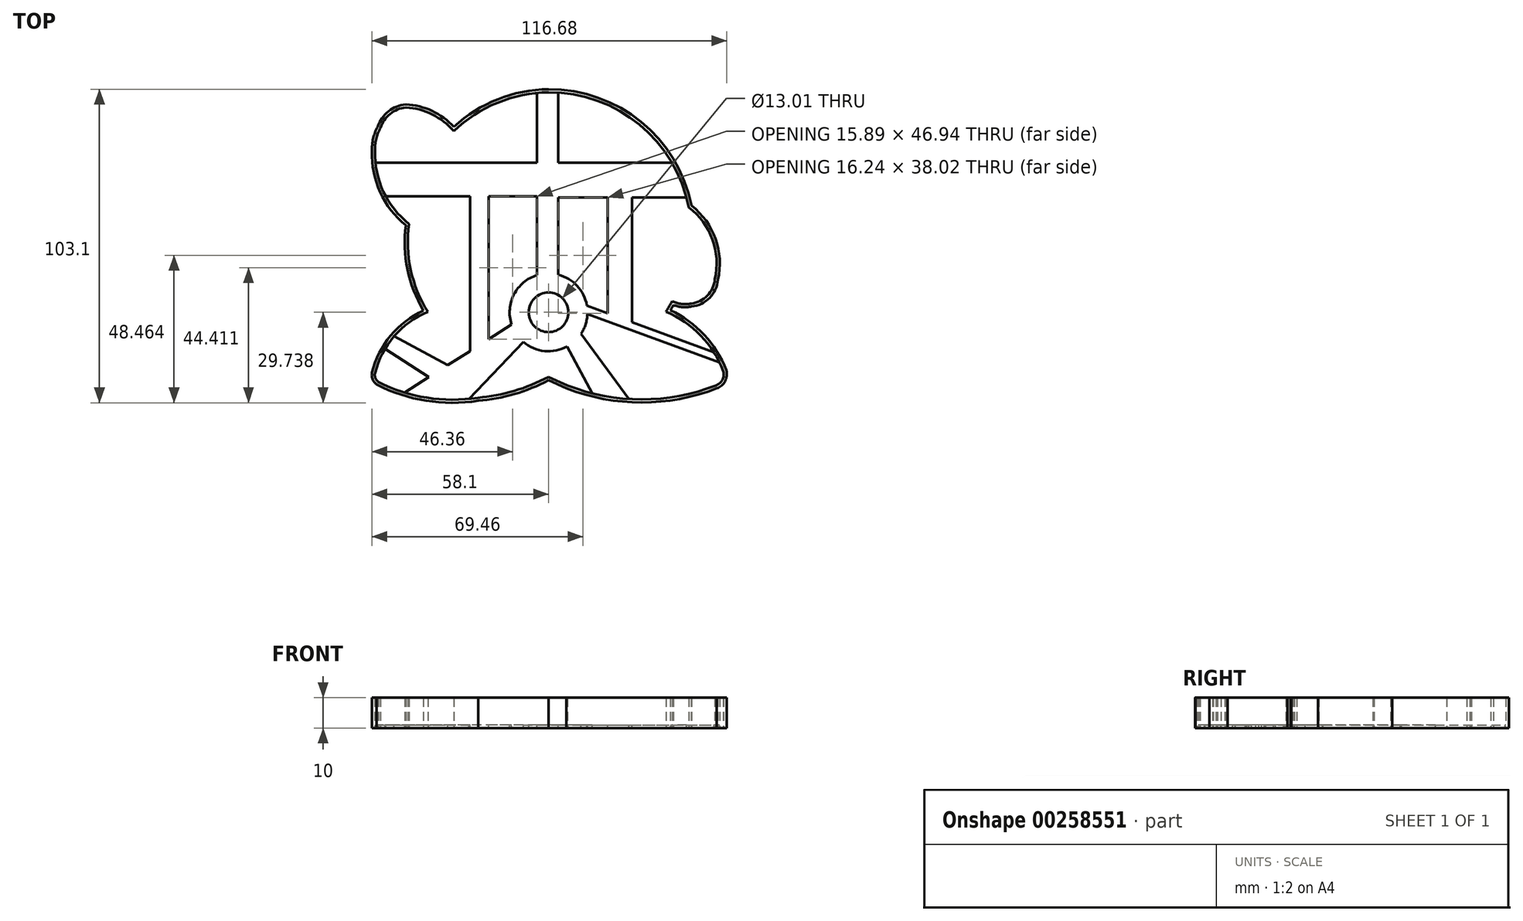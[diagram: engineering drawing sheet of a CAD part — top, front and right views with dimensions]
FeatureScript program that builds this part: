
annotation { "Feature Type Name" : "Feature", "Feature Type Description" : "" }
export const myFeature = defineFeature(function(context is Context, id is Id, definition is map)
    precondition{}
    {
        {
            var Q0;
            Q0=qCreatedBy(makeId("Top.planeOp"),FACE);
            var sketch = newSketch(context, id + "F0", { "sketchPlane" : qUnion([Q0])});
            skArc(sketch, "E0", {"start": v(0, 10.07) * mm, "mid": v(-2.37, 9.57) * mm, "end": v(-4.3, 8.09) * mm});
            skArc(sketch, "E1", {"start": v(4.44, 8.45) * mm, "mid": v(2.4, 9.73) * mm, "end": v(0, 10.07) * mm});
            skArc(sketch, "E2", {"start": v(0, 0) * mm, "mid": v(3.91, 3.34) * mm, "end": v(4.44, 8.45) * mm});
            skArc(sketch, "E3", {"start": v(-4.3, 8.09) * mm, "mid": v(-3.66, 3.24) * mm, "end": v(0, 0) * mm});
            skArc(sketch, "E4", {"start": v(4.25, 4.1) * mm, "mid": v(0.1, 6.4) * mm, "end": v(-4.06, 4.15) * mm});
            skSolve(sketch);
        }
        {
            var Q0;
            Q0=qCreatedBy(makeId("Top.planeOp"),FACE);
            var sketch = newSketch(context, id + "F1", { "sketchPlane" : qUnion([Q0])});
            skArc(sketch, "E5", {"start": v(0, 56.34) * mm, "mid": v(-18.69, 52.18) * mm, "end": v(-34.16, 40.9) * mm});
            skArc(sketch, "E6", {"start": v(47.02, 18.06) * mm, "mid": v(30.35, 45.6) * mm, "end": v(0, 56.34) * mm});
            skArc(sketch, "E7", {"start": v(55.64, -6.32) * mm, "mid": v(54.87, 7.12) * mm, "end": v(47.02, 18.06) * mm});
            skArc(sketch, "E8", {"start": v(47.02, -15.11) * mm, "mid": v(52.9, -12.26) * mm, "end": v(55.64, -6.32) * mm});
            skArc(sketch, "E9", {"start": v(38.57, -13.21) * mm, "mid": v(42.59, -15.09) * mm, "end": v(47.02, -15.11) * mm});
            skArc(sketch, "E10", {"start": v(0, -39.37) * mm, "mid": v(23.82, -32.45) * mm, "end": v(41.07, -14.62) * mm});
            skArc(sketch, "E11", {"start": v(58.4, -36.08) * mm, "mid": v(51.13, -24.45) * mm, "end": v(40.06, -16.36) * mm});
            skArc(sketch, "E12", {"start": v(55.3, -42.02) * mm, "mid": v(58.02, -39.66) * mm, "end": v(58.4, -36.08) * mm});
            skArc(sketch, "E13", {"start": v(5.87, -42.02) * mm, "mid": v(30.58, -46.66) * mm, "end": v(55.3, -42.02) * mm});
            skLineSegment(sketch, "E14", {"start": v(5.87, -42.02) * mm, "end": v(0, -39.37) * mm});
            skArc(sketch, "E15", {"start": v(-31.1, 44) * mm, "mid": v(-38.28, 49.2) * mm, "end": v(-46.9, 51.35) * mm});
            skArc(sketch, "E16", {"start": v(-46.9, 51.35) * mm, "mid": v(-52.61, 49.06) * mm, "end": v(-56.14, 44.01) * mm});
            skArc(sketch, "E17", {"start": v(-35.42, -22.83) * mm, "mid": v(-19.28, -34.46) * mm, "end": v(0, -39.37) * mm});
            skArc(sketch, "E18", {"start": v(-46.63, 13.39) * mm, "mid": v(-46.53, -2.02) * mm, "end": v(-41.11, -16.44) * mm});
            skArc(sketch, "E19", {"start": v(-35.42, -22.83) * mm, "mid": v(-38.15, -19.53) * mm, "end": v(-41.11, -16.44) * mm});
            skArc(sketch, "E20", {"start": v(-41.11, -16.44) * mm, "mid": v(-51.88, -24.7) * mm, "end": v(-58.01, -36.8) * mm});
            skArc(sketch, "E21", {"start": v(-23.18, -46.1) * mm, "mid": v(-11.25, -43.9) * mm, "end": v(0, -39.37) * mm});
            skArc(sketch, "E22", {"start": v(-56.46, -40.76) * mm, "mid": v(-40.24, -46.08) * mm, "end": v(-23.18, -46.1) * mm});
            skArc(sketch, "E23", {"start": v(-58.01, -36.8) * mm, "mid": v(-57.83, -39.01) * mm, "end": v(-56.46, -40.76) * mm});
            skArc(sketch, "E24", {"start": v(-58.01, 35.98) * mm, "mid": v(-55.3, 22.5) * mm, "end": v(-46.9, 11.61) * mm});
            skArc(sketch, "E25", {"start": v(-56.14, 44.01) * mm, "mid": v(-57.63, 40.13) * mm, "end": v(-58.01, 35.98) * mm});
            skSolve(sketch);
        }
        {
            var Q0;
            Q0=qCreatedBy(makeId("Top.planeOp"),FACE);
            var sketch = newSketch(context, id + "F2", { "sketchPlane" : qUnion([Q0])});
            skEllipse(sketch, "E26", {"center": v(48.28, -29.33) * mm, "majorRadius": 4.7 * mm, "minorRadius": 3.01 * mm, "majorAxis": v(0.73, -0.69)});
            skSolve(sketch);
        }
        {
            var Q0;
            Q0=qCreatedBy(makeId("Top.planeOp"),FACE);
            var sketch = newSketch(context, id + "F3", { "sketchPlane" : qUnion([Q0])});
            skEllipse(sketch, "E27", {"center": v(-48, -29.52) * mm, "majorRadius": 4.65 * mm, "minorRadius": 2.97 * mm, "majorAxis": v(0.74, 0.68)});
            skSolve(sketch);
        }
        {
            var Q0;
            Q0=qCreatedBy(makeId("Top.planeOp"),FACE);
            var sketch = newSketch(context, id + "F4", { "sketchPlane" : qUnion([Q0])});
            skEllipse(sketch, "E28", {"center": v(10.52, 30.66) * mm, "majorRadius": 5.49 * mm, "minorRadius": 3 * mm, "majorAxis": v(0, 1)});
            skEllipse(sketch, "E29", {"center": v(10.52, 23.34) * mm, "majorRadius": 12.86 * mm, "minorRadius": 4.34 * mm, "majorAxis": v(0, 1)});
            skPoint(sketch, "E29.centerSnap0", {"position": v(10.52, 25.17) * mm});
            skEllipse(sketch, "E30", {"center": v(-10.38, 30.69) * mm, "majorRadius": 5.47 * mm, "minorRadius": 2.96 * mm, "majorAxis": v(0, 1)});
            skEllipse(sketch, "E31", {"center": v(-10.52, 23.38) * mm, "majorRadius": 12.83 * mm, "minorRadius": 4.63 * mm, "majorAxis": v(0.03, 1)});
            skSolve(sketch);
        }
        {
            var Q0;
            Q0=qCreatedBy(makeId("Top.planeOp"),FACE);
            var sketch = newSketch(context, id + "F5", { "sketchPlane" : qUnion([Q0])});
            skEllipse(sketch, "E32", {"center": v(-23.7, 11.27) * mm, "majorRadius": 7.13 * mm, "minorRadius": 4.52 * mm, "majorAxis": v(0.98, -0.2)});
            skEllipse(sketch, "E33", {"center": v(23.97, 11.36) * mm, "majorRadius": 7.24 * mm, "minorRadius": 4.47 * mm, "majorAxis": v(0.98, 0.18)});
            skSolve(sketch);
        }
        {
            var Q0;
            {var subQ5=sQuery(id+"F1.wireOp",EDGE,"E6");Q0=makeQuery(id+"F1.imprint","IMPRINT",FACE,{"disambiguationData":[TD([[makeQuery(id+"F1.imprint","IMPRINT",EDGE,{"derivedFrom":subQ5}),1.0]])]});}
            var Q1;
            Q1=makeQuery(id+"F1.imprint","IMPRINT",FACE,{"disambiguationData":[TD([[makeQuery(id+"F1.imprint","IMPRINT",EDGE,{"derivedFrom":sQuery(id+"F1.wireOp",EDGE,"E17")}),-1.0]])]});
            var Q2;
            {var subQ0=sQuery(id+"F1.wireOp",EDGE,"E11");Q2=makeQuery(id+"F1.imprint","IMPRINT",FACE,{"disambiguationData":[TD([[makeQuery(id+"F1.imprint","IMPRINT",EDGE,{"derivedFrom":subQ0}),1.0]])]});}
            extrude(context, id + "F6", {"entities" : qUnion([Q0, Q1, Q2]), "depth" : 10 * mm});
        }
        {
            var Q0;
            Q0=makeQuery(id+"F6.opExtrude","CAP_FACE",FACE,{"disambiguationData":[OSD([sQuery(id+"F1.wireOp",EDGE,"E5"),sQuery(id+"F1.wireOp",EDGE,"E6"),sQuery(id+"F1.wireOp",EDGE,"E7"),sQuery(id+"F1.wireOp",EDGE,"E8"),sQuery(id+"F1.wireOp",EDGE,"E9"),sQuery(id+"F1.wireOp",EDGE,"E10"),sQuery(id+"F1.wireOp",EDGE,"E11"),sQuery(id+"F1.wireOp",EDGE,"E12"),sQuery(id+"F1.wireOp",EDGE,"E13"),sQuery(id+"F1.wireOp",EDGE,"E14"),sQuery(id+"F1.wireOp",EDGE,"E15"),sQuery(id+"F1.wireOp",EDGE,"E16"),sQuery(id+"F1.wireOp",EDGE,"E18"),sQuery(id+"F1.wireOp",EDGE,"E20"),sQuery(id+"F1.wireOp",EDGE,"E21"),sQuery(id+"F1.wireOp",EDGE,"E22"),sQuery(id+"F1.wireOp",EDGE,"E23"),sQuery(id+"F1.wireOp",EDGE,"E24"),sQuery(id+"F1.wireOp",EDGE,"E25")])],"isStart":false});
            shell(context, id + "F7", {"entities" : qUnion([Q0]), "thickness" : 1 * mm});
        }
        {
            var Q0;
            Q0=sQuery(id+"F1.wireOp",EDGE,"E17");
            extrude(context, id + "F8", {"bodyType" : ToolBodyType.SURFACE, "surfaceEntities" : qUnion([Q0]), "depth" : 6 * mm});
        }
        {
            var Q0;
            Q0=sQuery(id+"F1.wireOp",EDGE,"E19");
            extrude(context, id + "F9", {"bodyType" : ToolBodyType.SURFACE, "surfaceEntities" : qUnion([Q0]), "depth" : 6 * mm});
        }
        {
            var Q0;
            Q0=sQuery(id+"F3.wireOp",EDGE,"E27");
            extrude(context, id + "F10", {"bodyType" : ToolBodyType.SURFACE, "surfaceEntities" : qUnion([Q0]), "depth" : 6 * mm});
        }
        {
            var Q0;
            Q0=sQuery(id+"F2.wireOp",EDGE,"E26");
            extrude(context, id + "F11", {"bodyType" : ToolBodyType.SURFACE, "surfaceEntities" : qUnion([Q0]), "depth" : 6 * mm});
        }
        {
            var Q0;
            Q0=sQuery(id+"F1.wireOp",EDGE,"E10");
            extrude(context, id + "F12", {"bodyType" : ToolBodyType.SURFACE, "surfaceEntities" : qUnion([Q0]), "depth" : 6 * mm});
        }
        {
            var Q0;
            Q0=sQuery(id+"F5.wireOp",EDGE,"E33");
            var Q1;
            Q1=sQuery(id+"F5.wireOp",EDGE,"E32");
            extrude(context, id + "F13", {"bodyType" : ToolBodyType.SURFACE, "surfaceEntities" : qUnion([Q0, Q1]), "depth" : 6 * mm});
        }
        {
            var Q0;
            Q0=sQuery(id+"F4.wireOp",EDGE,"E28");
            extrude(context, id + "F14", {"bodyType" : ToolBodyType.SURFACE, "surfaceEntities" : qUnion([Q0]), "depth" : 6 * mm});
        }
        {
            var Q0;
            Q0=sQuery(id+"F4.wireOp",EDGE,"E30");
            extrude(context, id + "F15", {"bodyType" : ToolBodyType.SURFACE, "surfaceEntities" : qUnion([Q0]), "depth" : 6 * mm});
        }
        {
            var Q0;
            Q0=sQuery(id+"F4.wireOp",EDGE,"E29");
            extrude(context, id + "F16", {"bodyType" : ToolBodyType.SURFACE, "surfaceEntities" : qUnion([Q0]), "depth" : 6 * mm});
        }
        {
            var Q0;
            Q0=sQuery(id+"F4.wireOp",EDGE,"E31");
            extrude(context, id + "F17", {"bodyType" : ToolBodyType.SURFACE, "surfaceEntities" : qUnion([Q0]), "depth" : 6 * mm});
        }
        {
            var Q0;
            Q0=sQuery(id+"F0.wireOp",EDGE,"E0");
            var Q1;
            Q1=sQuery(id+"F0.wireOp",EDGE,"E1");
            extrude(context, id + "F18", {"bodyType" : ToolBodyType.SURFACE, "surfaceEntities" : qUnion([Q0, Q1]), "depth" : 6 * mm});
        }
        {
            var Q0;
            Q0=sQuery(id+"F0.wireOp",EDGE,"E2");
            var Q1;
            Q1=sQuery(id+"F0.wireOp",EDGE,"E3");
            extrude(context, id + "F19", {"bodyType" : ToolBodyType.SURFACE, "surfaceEntities" : qUnion([Q0, Q1]), "depth" : 6 * mm});
        }
        {
            var Q0;
            Q0=sQuery(id+"F0.wireOp",EDGE,"E4");
            extrude(context, id + "F20", {"bodyType" : ToolBodyType.SURFACE, "surfaceEntities" : qUnion([Q0]), "depth" : 6 * mm});
        }
        {
            var Q0;
            Q0=makeQuery(id+"F7.opShell","OFFSET_FACE",FACE,{"disambiguationData":[OSD([sQuery(id+"F1.wireOp",EDGE,"E5"),sQuery(id+"F1.wireOp",EDGE,"E6"),sQuery(id+"F1.wireOp",EDGE,"E7"),sQuery(id+"F1.wireOp",EDGE,"E8"),sQuery(id+"F1.wireOp",EDGE,"E9"),sQuery(id+"F1.wireOp",EDGE,"E10"),sQuery(id+"F1.wireOp",EDGE,"E11"),sQuery(id+"F1.wireOp",EDGE,"E12"),sQuery(id+"F1.wireOp",EDGE,"E13"),sQuery(id+"F1.wireOp",EDGE,"E14"),sQuery(id+"F1.wireOp",EDGE,"E15"),sQuery(id+"F1.wireOp",EDGE,"E16"),sQuery(id+"F1.wireOp",EDGE,"E18"),sQuery(id+"F1.wireOp",EDGE,"E20"),sQuery(id+"F1.wireOp",EDGE,"E21"),sQuery(id+"F1.wireOp",EDGE,"E22"),sQuery(id+"F1.wireOp",EDGE,"E23"),sQuery(id+"F1.wireOp",EDGE,"E24"),sQuery(id+"F1.wireOp",EDGE,"E25")])]});
            var sketch = newSketch(context, id + "F21", { "sketchPlane" : qUnion([Q0])});
            skCircle(sketch, "E34", {"center": v(0, -17.02) * mm, "radius": 12.8 * mm});
            skLineSegment(sketch, "E35", {"start": v(-3.8, -4.8) * mm, "end": v(-3.8, 55.13) * mm});
            skLineSegment(sketch, "E36", {"start": v(3.24, -4.65) * mm, "end": v(3.24, 55.34) * mm});
            skLineSegment(sketch, "E37", {"start": v(3.24, 32.2) * mm, "end": v(40.56, 32.2) * mm});
            skLineSegment(sketch, "E38", {"start": v(3.24, 20.71) * mm, "end": v(45.37, 20.71) * mm});
            skLineSegment(sketch, "E39", {"start": v(12.59, -14.75) * mm, "end": v(54.33, -30.22) * mm});
            skLineSegment(sketch, "E40", {"start": v(12.78, -17.62) * mm, "end": v(56.19, -33.52) * mm});
            skLineSegment(sketch, "E41", {"start": v(19.48, 20.71) * mm, "end": v(19.48, -17.3) * mm});
            skLineSegment(sketch, "E42", {"start": v(27.48, 20.71) * mm, "end": v(27.48, -20.27) * mm});
            skLineSegment(sketch, "E43", {"start": v(14.36, -43.67) * mm, "end": v(6.14, -28.24) * mm});
            skLineSegment(sketch, "E44", {"start": v(10.7, -24.02) * mm, "end": v(26.47, -45.53) * mm});
            skLineSegment(sketch, "E45", {"start": v(-8.3, -26.76) * mm, "end": v(-26.2, -45.49) * mm});
            skLineSegment(sketch, "E46", {"start": v(-12.15, -21.01) * mm, "end": v(-47.26, -43.42) * mm});
            skLineSegment(sketch, "E47", {"start": v(-50.74, -24.9) * mm, "end": v(-33.18, -34.43) * mm});
            skLineSegment(sketch, "E48", {"start": v(-53.75, -29.07) * mm, "end": v(-39.3, -38.34) * mm});
            skLineSegment(sketch, "E49", {"start": v(-3.8, 21.12) * mm, "end": v(-53.5, 21.12) * mm});
            skLineSegment(sketch, "E50", {"start": v(-3.8, 32.2) * mm, "end": v(-56.89, 32.2) * mm});
            skLineSegment(sketch, "E51", {"start": v(-19.69, 21.12) * mm, "end": v(-19.69, -25.82) * mm});
            skLineSegment(sketch, "E52", {"start": v(-25.84, 21.12) * mm, "end": v(-25.84, -29.75) * mm});
            skSolve(sketch);
        }
        {
            var Q0;
            {var subQ0=sQuery(id+"F21.wireOp",EDGE,"E42");Q0=makeQuery(id+"F21.imprint","IMPRINT",FACE,{"disambiguationData":[TD([[makeQuery(id+"F21.imprint","IMPRINT",EDGE,{"derivedFrom":subQ0}),1.0]])]});}
            var Q1;
            {var subQ3=sQuery(id+"F21.wireOp",EDGE,"E41");Q1=makeQuery(id+"F21.imprint","IMPRINT",FACE,{"disambiguationData":[TD([[makeQuery(id+"F21.imprint","IMPRINT",EDGE,{"derivedFrom":subQ3}),-1.0]])]});}
            var Q2;
            {var subQ0=sQuery(id+"F21.wireOp",EDGE,"E37");Q2=makeQuery(id+"F21.imprint","IMPRINT",FACE,{"disambiguationData":[TD([[makeQuery(id+"F21.imprint","IMPRINT",EDGE,{"derivedFrom":subQ0}),1.0]])]});}
            var Q3;
            {var subQ7=sQuery(id+"F21.wireOp",EDGE,"E50");Q3=makeQuery(id+"F21.imprint","IMPRINT",FACE,{"disambiguationData":[TD([[makeQuery(id+"F21.imprint","IMPRINT",EDGE,{"derivedFrom":subQ7}),-1.0]])]});}
            var Q4;
            {var subQ3=sQuery(id+"F21.wireOp",EDGE,"E51");Q4=makeQuery(id+"F21.imprint","IMPRINT",FACE,{"disambiguationData":[TD([[makeQuery(id+"F21.imprint","IMPRINT",EDGE,{"derivedFrom":subQ3}),1.0]])]});}
            var Q5;
            {var subQ5=sQuery(id+"F21.wireOp",EDGE,"E47");Q5=makeQuery(id+"F21.imprint","IMPRINT",FACE,{"disambiguationData":[TD([[makeQuery(id+"F21.imprint","IMPRINT",EDGE,{"derivedFrom":subQ5}),1.0]])]});}
            var Q6;
            {var subQ4=sQuery(id+"F21.wireOp",EDGE,"E48");Q6=makeQuery(id+"F21.imprint","IMPRINT",FACE,{"disambiguationData":[TD([[makeQuery(id+"F21.imprint","IMPRINT",EDGE,{"derivedFrom":subQ4}),-1.0]])]});}
            var Q7;
            {var subQ5=sQuery(id+"F21.wireOp",EDGE,"E43");Q7=makeQuery(id+"F21.imprint","IMPRINT",FACE,{"disambiguationData":[TD([[makeQuery(id+"F21.imprint","IMPRINT",EDGE,{"derivedFrom":subQ5}),1.0]])]});}
            var Q8;
            {var subQ5=sQuery(id+"F21.wireOp",EDGE,"E40");Q8=makeQuery(id+"F21.imprint","IMPRINT",FACE,{"disambiguationData":[TD([[makeQuery(id+"F21.imprint","IMPRINT",EDGE,{"derivedFrom":subQ5}),-1.0]])]});}
            extrude(context, id + "F22", {"entities" : qUnion([Q0, Q1, Q2, Q3, Q4, Q5, Q6, Q7, Q8]), "operationType" : NewBodyOperationType.REMOVE, "oppositeDirection" : true, "depth" : 25 * mm});
        }
        {
            var Q0;
            Q0=makeQuery(id+"F7.opShell","OFFSET_FACE",FACE,{"disambiguationData":[OSD([sQuery(id+"F1.wireOp",EDGE,"E5"),sQuery(id+"F1.wireOp",EDGE,"E6"),sQuery(id+"F1.wireOp",EDGE,"E7"),sQuery(id+"F1.wireOp",EDGE,"E8"),sQuery(id+"F1.wireOp",EDGE,"E9"),sQuery(id+"F1.wireOp",EDGE,"E10"),sQuery(id+"F1.wireOp",EDGE,"E11"),sQuery(id+"F1.wireOp",EDGE,"E12"),sQuery(id+"F1.wireOp",EDGE,"E13"),sQuery(id+"F1.wireOp",EDGE,"E14"),sQuery(id+"F1.wireOp",EDGE,"E15"),sQuery(id+"F1.wireOp",EDGE,"E16"),sQuery(id+"F1.wireOp",EDGE,"E18"),sQuery(id+"F1.wireOp",EDGE,"E20"),sQuery(id+"F1.wireOp",EDGE,"E21"),sQuery(id+"F1.wireOp",EDGE,"E22"),sQuery(id+"F1.wireOp",EDGE,"E23"),sQuery(id+"F1.wireOp",EDGE,"E24"),sQuery(id+"F1.wireOp",EDGE,"E25")])]});
            var sketch = newSketch(context, id + "F23", { "sketchPlane" : qUnion([Q0])});
            skCircle(sketch, "E53", {"center": v(0, -17.02) * mm, "radius": 6.5 * mm});
            skSolve(sketch);
        }
        {
            var Q0;
            Q0 = qSketchRegion(id + "F23", true);
            extrude(context, id + "F24", {"entities" : qUnion([Q0]), "operationType" : NewBodyOperationType.REMOVE, "oppositeDirection" : true, "depth" : 25 * mm});
        }
    });
